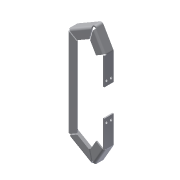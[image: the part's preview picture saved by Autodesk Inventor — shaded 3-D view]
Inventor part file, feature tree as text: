
AUTODESK INVENTOR PART (.ipt)
format: ipt  version: 2015 (Build 190159000, 159)  size: 296,448 bytes
history: native  units: in
note: dims shown in document units (in); Inventor stores cm internally (conversion verified against a paired STEP export)
features: sheet_metal_op x6, other x3, sketch x2, hole x1, reference x1
ambient origin geometry x8: Origin, YZ Plane, XZ Plane, XY Plane, X Axis, Y Axis, Z Axis, Center Point
bodies: Solid1 (feature_tree)
feature tree (13):
  sheet_metal_op  "Contour Flange1"
  sheet_metal_op  "Flange2"
  hole  "Hole1"  [1 undecoded]
  reference  "Reference1"
  other  "Plate1"
  sheet_metal_op  "Bend1"
  sheet_metal_op  "Corner1"
  sketch  "Sketch3"  dims[d0=120.0deg d2=4.0in]
  other  "Plate3"
  sheet_metal_op  "Bend3"
  sheet_metal_op  "Corner3"
  sketch  "Sketch4"  dims[d3=3.0in d4=0.125in d5=0.0625in d6=0.25in d7=0.125in d8=1.0in d9=0.125in d10=0.125in d11=0.5in d12=0.125in d13=0.125in d24=0.125in d25=0.0625in d26=0.25in d27=0.125in d28=1.0in d29=90.0deg d30=0.125in d31=0.5in d32=0.125in d33=0.125in d34=0.25in d35=0.75in d36=0.375in d37=0.25in d38=0.5635in d39=0.125in d40=0.8108in d43=1.47in]
  other  "Definition1"
note: 1 required parameter value undecoded (feature->parameter linkage not recoverable at this tier; creation-order binding heuristic only, values carry confidence <= 0.55)
